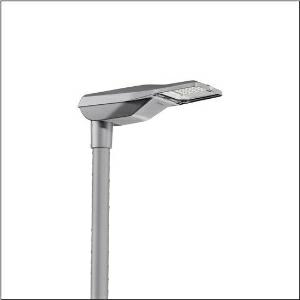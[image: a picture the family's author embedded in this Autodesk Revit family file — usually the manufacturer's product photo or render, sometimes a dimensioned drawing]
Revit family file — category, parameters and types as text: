
# Revit family: streetlight_sl_21_iq_micro___st1_0a_5xe1d31d08cb_abfe
name_source: partatom
category: Lighting Fixtures
units: mm (PartAtom-declared; Revit-internal decimal feet)

## family parameters
Cut with Voids When Loaded = No
Host = Face
Light Source = No
Part Type = Normal
Room Calculation Point = No
Round Connector Dimension = Use Diameter
Shared = No

## types (1)
- --- (1 x LED, 2870 lm, 19.4 W, 3000K)
    Apparent Load = 19 VA
    CIE Flux Codes = 37 72 97 100 100
    Color Rendering = 70
    Color Temperature = 3000K
    Default Elevation = 1800 mm
    Description = Streetlight SL 21 iQ micro, mast luminaire, primary light control with lens, of PMMA, primary optical cover: cover, of toughened safety glass, transparent, light distribution: ST1.0a, light emission: direct distribution, primary light characteristic: asymmetric, installation type: post-top, side-entry, LED, High Power LED, rated luminous flux: 2.870lm, luminous efficacy: 148lm/W, light colour: 730, colour temperature: 3000K, control gear: iQ-Comfort, control: Auto-Match, Temp-Guard, Lumen-Switch, Night-Set, Smart-Wire, Light-Fading, Desk-Remote (wireless, voltage-free reading and setting of iQ features in the workshop via application-optimized NFC function/RFID function), optimised constant luminous flux control (CLO 2.0), pre-setting: linear dimming characteristic, mains connection: 220..240V, AC, 50/60Hz, start of lifetime: 19W, end of service life: 20W, reduction: 10W, luminaire housing, of diecast aluminium, powder-coated, Siteco® metallic grey (DB 702S), corrosivity category C5 mid according to DIN EN ISO 12944, please order mast flange separately, inclination adjustable: 0°, 5°, 10°, 15°, sealing non-destructively replaceable, multi-level sealing system, length: 528mm, width: 235mm, height: 110mm, mast flange for spigot size: 42mm (side-entry): 5XC10008XM4, 60/48mm (side-entry/post-top): 5XC10108XM2, 76/60mm (side-entry/post-top): 5XC10108XM1, protection rating (complete): IP66, insulation class (complete): insulation class II (safety insulation), certification: CE, ENEC, ENEC+, VDE, impact resistance: IK10, permissible operating ambient temperature for outdoor applications: -40..+50°C, standard-compliant lighting for roads and squares, packaging unit: 1 piece

Light Distribution: ST1.0a
    Height = 110 mm
    Lamp = 1 x LED
    Lamp Light Flux = 2870 lm
    Lamp Power = 19.4 W
    Lamp count = 1
    Length = 528 mm
    Luminous efficacy = 148 lm/W
    Manufacturer = Siteco
    ModVariant = No
    Model = 5XE1D31D08CB
    Number of Poles = 1
    OnlyDefault = Yes
    Power Factor = 1
    Product Name = Streetlight SL 21 iQ micro | ST1.0a
    Product group = mast luminaire | pylon top
    ProductGroupID = 6100
    Protection Class = Protection class II
    Protection Degree = IP 66
    RLX_Detail_Level = 1
    RLX_Emergency_Light_Flux = 0 lm
    RLX_Emergency_Type = 0
    RLX_Emergency_Type_DB = No
    RlxData = <blob elided: 98853 chars, md5=d3b83011>
    Socket = socket
    Standby Power = 0 W
    System Light Flux = 2870 lm
    System Power = 19 W
    Type Comments = factory setting: luminous flux: 100 % | dim-lin: 254 | 387 mA
    Type Image = l_1006881.jpg
    URL = http://relux.com
    VarID = @adj_139288
    Voltage = 0 V
    Weight = 0.00 kg
    Width = 235 mm

## geometry (parser evidence)
native form markers: Blend x4, Sweep x10
no freeform markers — native parametric forms only
